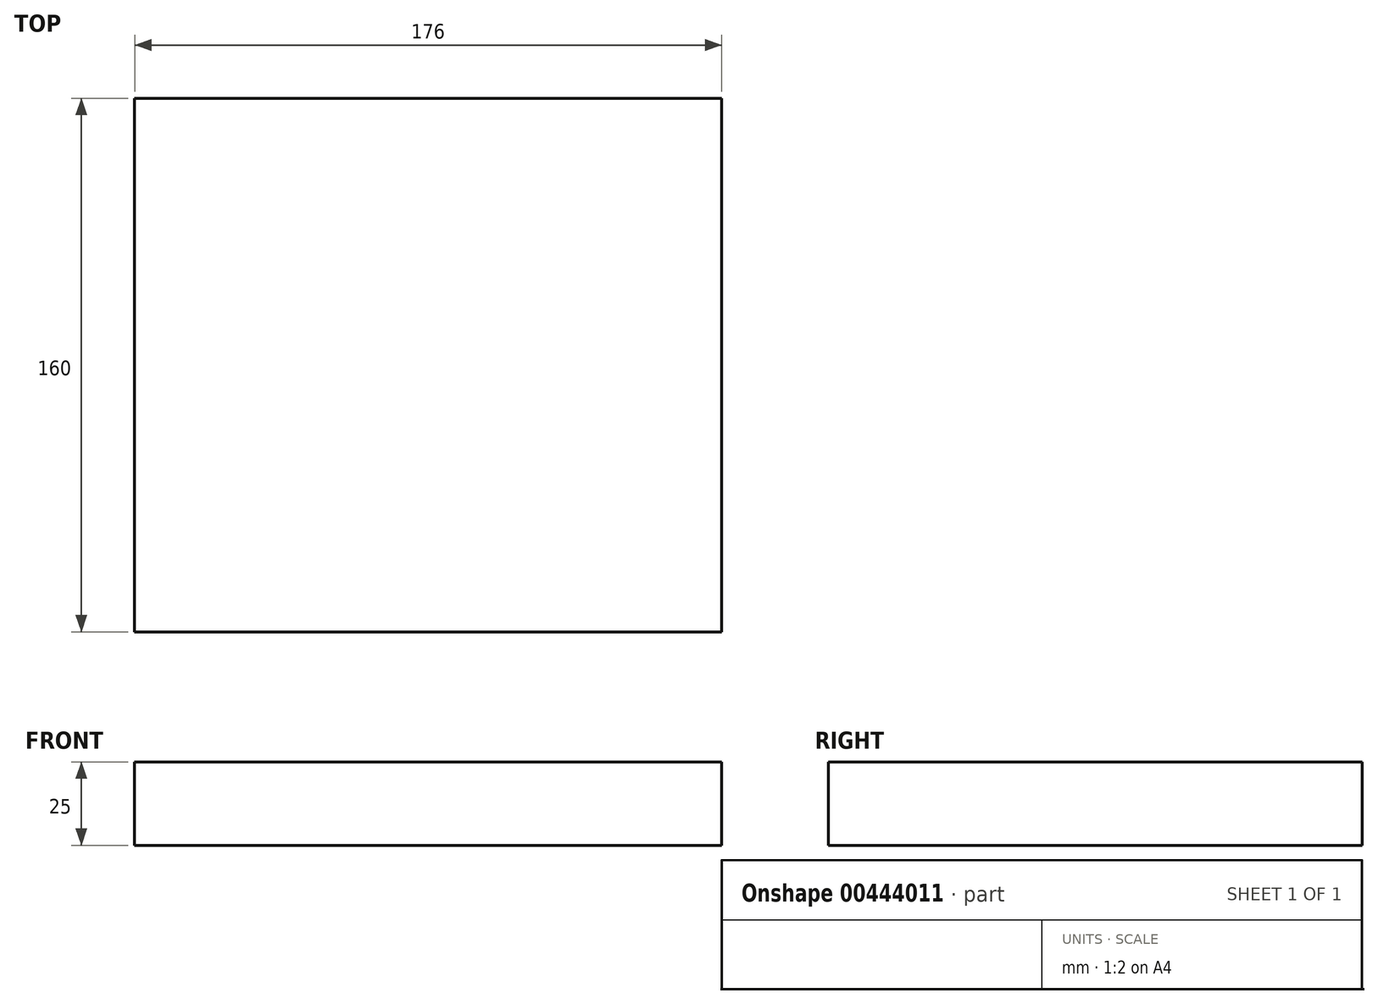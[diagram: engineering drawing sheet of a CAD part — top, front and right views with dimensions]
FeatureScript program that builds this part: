
annotation { "Feature Type Name" : "Feature", "Feature Type Description" : "" }
export const myFeature = defineFeature(function(context is Context, id is Id, definition is map)
    precondition{}
    {
        {
            var Q0;
            Q0=qCreatedBy(makeId("Top.planeOp"),FACE);
            var sketch = newSketch(context, id + "F0", { "sketchPlane" : qUnion([Q0])});
            skLineSegment(sketch, "E0.bottom", {"start": v(-73.65, -62.26) * mm, "end": v(102.35, -62.26) * mm});
            skLineSegment(sketch, "E0.top", {"start": v(-73.65, 97.74) * mm, "end": v(102.35, 97.74) * mm});
            skLineSegment(sketch, "E0.left", {"start": v(-73.65, -62.26) * mm, "end": v(-73.65, 97.74) * mm});
            skLineSegment(sketch, "E0.right", {"start": v(102.35, -62.26) * mm, "end": v(102.35, 97.74) * mm});
            skSolve(sketch);
        }
        {
            var Q0;
            Q0 = qSketchRegion(id + "F0", true);
            extrude(context, id + "F1", {"entities" : qUnion([Q0]), "depth" : 25 * mm});
        }
    });
